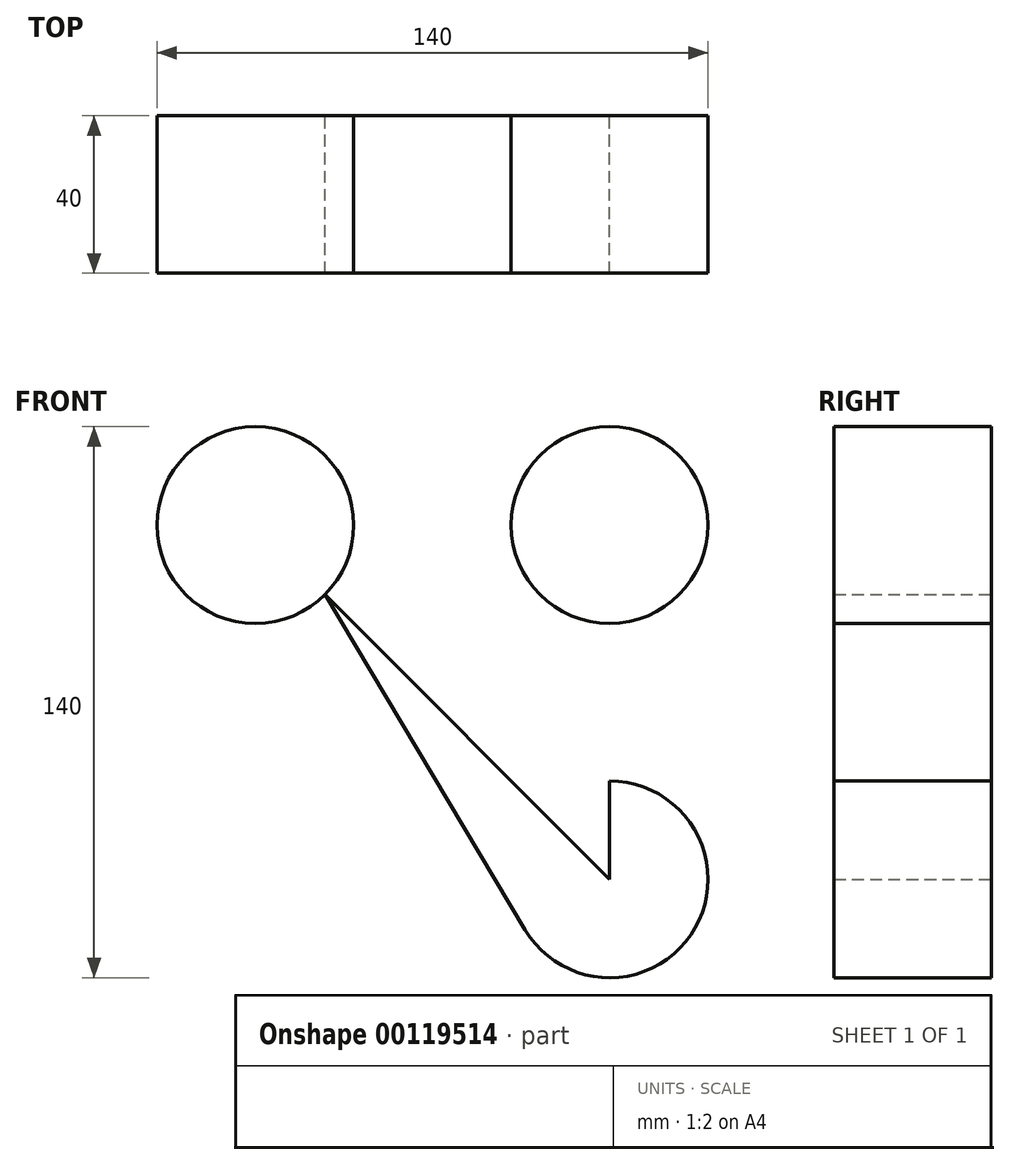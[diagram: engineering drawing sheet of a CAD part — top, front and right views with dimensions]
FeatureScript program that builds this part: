
annotation { "Feature Type Name" : "Feature", "Feature Type Description" : "" }
export const myFeature = defineFeature(function(context is Context, id is Id, definition is map)
    precondition{}
    {
        {
            var Q0;
            Q0=qCreatedBy(makeId("Front.planeOp"),FACE);
            var sketch = newSketch(context, id + "F0", { "sketchPlane" : qUnion([Q0])});
            skCircle(sketch, "E0", {"center": v(0, 0) * mm, "radius": 25 * mm});
            skCircle(sketch, "E1", {"center": v(0, 90) * mm, "radius": 25 * mm});
            skCircle(sketch, "E2", {"center": v(-90, 90) * mm, "radius": 25 * mm});
            skLineSegment(sketch, "E3", {"start": v(0, 0) * mm, "end": v(-90, 90) * mm});
            skLineSegment(sketch, "E4", {"start": v(-90, 90) * mm, "end": v(0, 90) * mm, "construction": true});
            skLineSegment(sketch, "E5", {"start": v(0, 90) * mm, "end": v(0, 0) * mm});
            skLineSegment(sketch, "E6", {"start": v(-72.32, 72.32) * mm, "end": v(-21.46, -12.82) * mm});
            skSolve(sketch);
        }
        {
            var Q0;
            Q0=makeQuery(id+"F0.imprint","IMPRINT",FACE,{"disambiguationData":[TD([[makeQuery(id+"F0.imprint","IMPRINT",EDGE,{"derivedFrom":sQuery(id+"F0.wireOp",EDGE,"E2")}),1.0]])]});
            var Q1;
            Q1=makeQuery(id+"F0.imprint","IMPRINT",FACE,{"disambiguationData":[TD([[makeQuery(id+"F0.imprint","IMPRINT",EDGE,{"derivedFrom":sQuery(id+"F0.wireOp",EDGE,"E1")}),1.0]])]});
            var Q2;
            {var subQ0=sQuery(id+"F0.wireOp",EDGE,"E0");var subQ1=makeQuery(id+"F0.imprint","INTERSECT",VERTEX,{"derivedFrom":[subQ0,sQuery(id+"F0.wireOp",EDGE,"E6")]});Q2=makeQuery(id+"F0.imprint","IMPRINT",FACE,{"disambiguationData":[TD([[makeQuery(id+"F0.imprint","IMPRINT",EDGE,{"disambiguationData":[TD([[subQ1,1.0]])],"derivedFrom":subQ0}),1.0]])]});}
            var Q3;
            {var subQ0=sQuery(id+"F0.wireOp",EDGE,"E6");Q3=makeQuery(id+"F0.imprint","IMPRINT",FACE,{"disambiguationData":[TD([[makeQuery(id+"F0.imprint","IMPRINT",EDGE,{"derivedFrom":subQ0}),1.0]])]});}
            extrude(context, id + "F1", {"entities" : qUnion([Q0, Q1, Q2, Q3]), "endBound" : BoundingType.SYMMETRIC, "depth" : 40 * mm});
        }
    });
